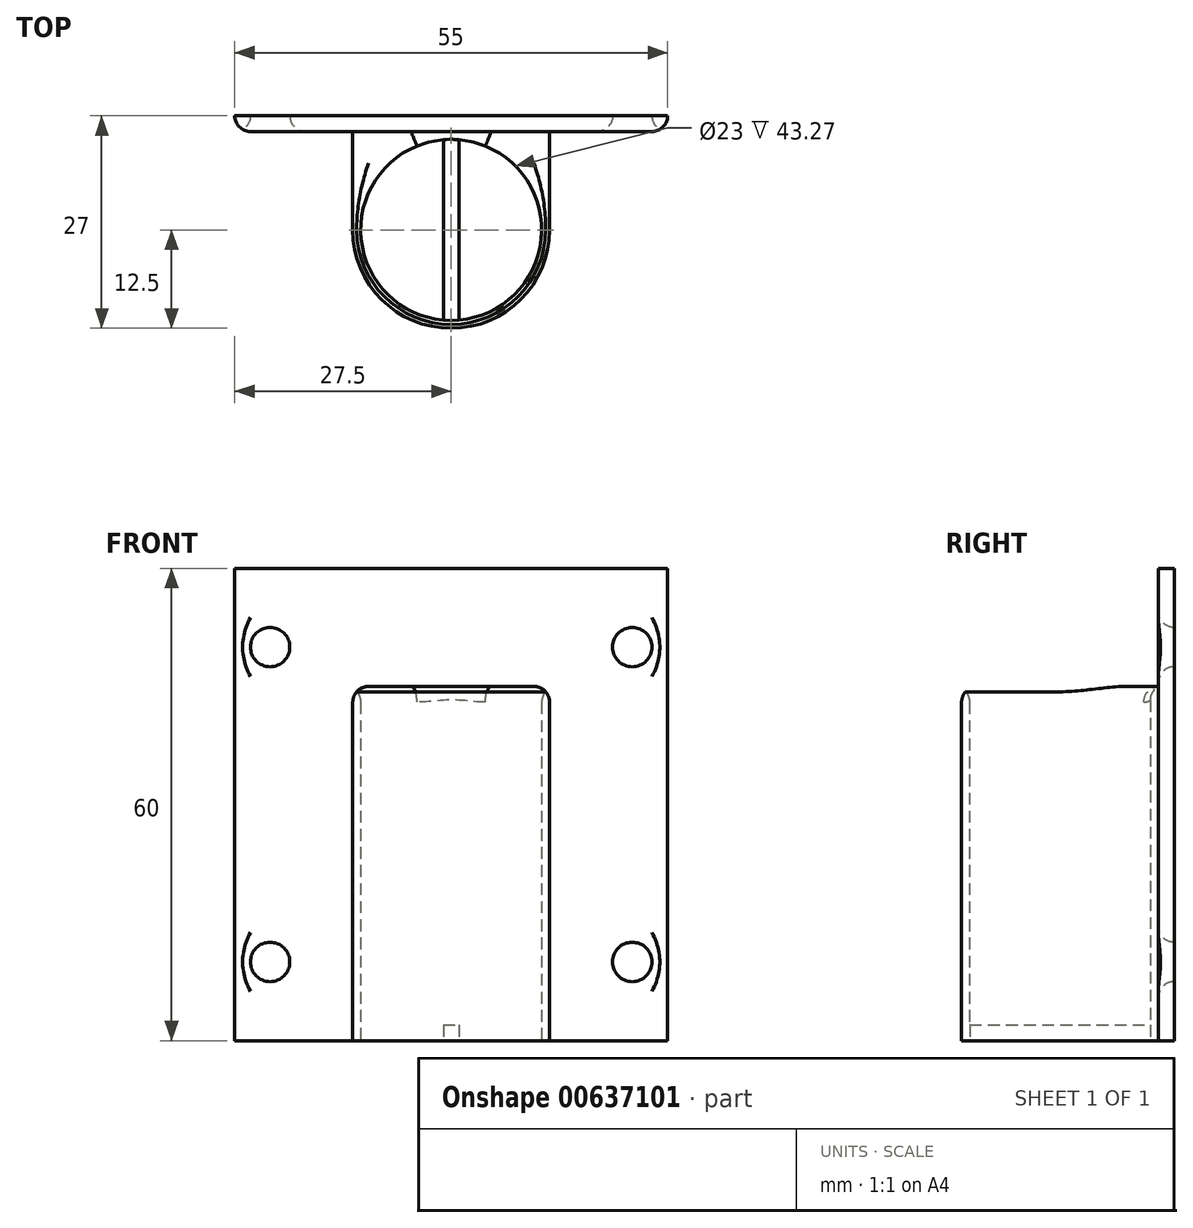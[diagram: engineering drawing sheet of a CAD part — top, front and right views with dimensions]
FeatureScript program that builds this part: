
annotation { "Feature Type Name" : "Feature", "Feature Type Description" : "" }
export const myFeature = defineFeature(function(context is Context, id is Id, definition is map)
    precondition{}
    {
        {
            var Q0;
            Q0=qCreatedBy(makeId("Top.planeOp"),FACE);
            var sketch = newSketch(context, id + "F0", { "sketchPlane" : qUnion([Q0])});
            skCircle(sketch, "E0", {"center": v(0, 0) * mm, "radius": 11.5 * mm});
            skCircle(sketch, "E1", {"center": v(0, 0) * mm, "radius": 12.5 * mm});
            skLineSegment(sketch, "E2", {"start": v(-12.5, 0) * mm, "end": v(-12.5, 14.5) * mm});
            skLineSegment(sketch, "E3", {"start": v(-12.5, 14.5) * mm, "end": v(27.5, 14.5) * mm});
            skLineSegment(sketch, "E4", {"start": v(12.5, 0) * mm, "end": v(12.5, 14.5) * mm});
            skLineSegment(sketch, "E5", {"start": v(-12.5, 14.5) * mm, "end": v(-27.5, 14.5) * mm});
            skLineSegment(sketch, "E6", {"start": v(-27.5, 14.5) * mm, "end": v(-27.5, 12.5) * mm});
            skLineSegment(sketch, "E7", {"start": v(27.5, 14.5) * mm, "end": v(27.5, 12.5) * mm});
            skLineSegment(sketch, "E8", {"start": v(-27.5, 12.5) * mm, "end": v(27.5, 12.5) * mm});
            skSolve(sketch);
        }
        {
            var Q0;
            {var subQ0=sQuery(id+"F0.wireOp",EDGE,"E5");Q0=makeQuery(id+"F0.imprint","IMPRINT",FACE,{"disambiguationData":[TD([[makeQuery(id+"F0.imprint","IMPRINT",EDGE,{"derivedFrom":subQ0}),1.0]])]});}
            var Q1;
            {var subQ4=sQuery(id+"F0.wireOp",EDGE,"E4");var subQ5=sQuery(id+"F0.wireOp",EDGE,"E3");var subQ6=makeQuery(id+"F0.imprint","INTERSECT",VERTEX,{"derivedFrom":[subQ5,subQ4]});Q1=makeQuery(id+"F0.imprint","IMPRINT",FACE,{"disambiguationData":[TD([[makeQuery(id+"F0.imprint","IMPRINT",EDGE,{"disambiguationData":[TD([[subQ6,1.0]])],"derivedFrom":subQ4}),1.0]])]});}
            var Q2;
            {var subQ0=sQuery(id+"F0.wireOp",EDGE,"E7");Q2=makeQuery(id+"F0.imprint","IMPRINT",FACE,{"disambiguationData":[TD([[makeQuery(id+"F0.imprint","IMPRINT",EDGE,{"derivedFrom":subQ0}),-1.0]])]});}
            var Q3;
            {var subQ0=sQuery(id+"F0.wireOp",EDGE,"E4");var subQ1=sQuery(id+"F0.wireOp",EDGE,"E1");var subQ2=makeQuery(id+"F0.imprint","INTERSECT",VERTEX,{"derivedFrom":[subQ1,subQ0]});Q3=makeQuery(id+"F0.imprint","IMPRINT",FACE,{"disambiguationData":[TD([[makeQuery(id+"F0.imprint","IMPRINT",EDGE,{"disambiguationData":[TD([[subQ2,-1.0]])],"derivedFrom":subQ1}),-1.0]])]});}
            var Q4;
            {var subQ0=sQuery(id+"F0.wireOp",EDGE,"E2");var subQ1=sQuery(id+"F0.wireOp",EDGE,"E1");var subQ2=makeQuery(id+"F0.imprint","INTERSECT",VERTEX,{"derivedFrom":[subQ1,subQ0]});Q4=makeQuery(id+"F0.imprint","IMPRINT",FACE,{"disambiguationData":[TD([[makeQuery(id+"F0.imprint","IMPRINT",EDGE,{"disambiguationData":[TD([[subQ2,1.0]])],"derivedFrom":subQ1}),-1.0]])]});}
            var Q5;
            Q5=makeQuery(id+"F0.imprint","IMPRINT",FACE,{"disambiguationData":[TD([[makeQuery(id+"F0.imprint","IMPRINT",EDGE,{"derivedFrom":sQuery(id+"F0.wireOp",EDGE,"E0")}),-1.0]])]});
            extrude(context, id + "F1", {"entities" : qUnion([Q0, Q1, Q2, Q3, Q4, Q5]), "depth" : 45 * mm, "offsetDistance" : 25 * mm});
        }
        {
            var Q0;
            Q0=makeQuery(id+"F1.opExtrude","CAP_FACE",FACE,{"disambiguationData":[OSD([sQuery(id+"F0.wireOp",EDGE,"E0"),sQuery(id+"F0.wireOp",EDGE,"E1"),sQuery(id+"F0.wireOp",EDGE,"E2"),sQuery(id+"F0.wireOp",EDGE,"E3"),sQuery(id+"F0.wireOp",EDGE,"E4"),sQuery(id+"F0.wireOp",EDGE,"E5"),sQuery(id+"F0.wireOp",EDGE,"E6"),sQuery(id+"F0.wireOp",EDGE,"E7"),sQuery(id+"F0.wireOp",EDGE,"E8")])],"isStart":false});
            var sketch = newSketch(context, id + "F2", { "sketchPlane" : qUnion([Q0])});
            skLineSegment(sketch, "E9", {"start": v(-27.5, 14.5) * mm, "end": v(27.5, 14.5) * mm});
            skLineSegment(sketch, "E10", {"start": v(27.5, 14.5) * mm, "end": v(27.5, 12.5) * mm});
            skLineSegment(sketch, "E11", {"start": v(27.5, 12.5) * mm, "end": v(-27.5, 12.5) * mm});
            skLineSegment(sketch, "E12", {"start": v(-27.5, 12.5) * mm, "end": v(-27.5, 14.5) * mm});
            skSolve(sketch);
        }
        {
            var Q0;
            Q0=makeQuery(id+"F2.imprint","IMPRINT",FACE,{"disambiguationData":[TD([[makeQuery(id+"F2.imprint","IMPRINT",EDGE,{"derivedFrom":sQuery(id+"F2.wireOp",EDGE,"E9")}),1.0]])]});
            extrude(context, id + "F3", {"entities" : qUnion([Q0]), "operationType" : NewBodyOperationType.ADD, "depth" : 15 * mm, "offsetDistance" : 25 * mm});
        }
        {
            var Q0;
            Q0=makeQuery(id+"F1.opExtrude","SWEPT_FACE",FACE,{"disambiguationData":[OSD([sQuery(id+"F0.wireOp",EDGE,"E3"),sQuery(id+"F0.wireOp",EDGE,"E5")])]});
            var sketch = newSketch(context, id + "F4", { "sketchPlane" : qUnion([Q0])});
            skCircle(sketch, "E13", {"center": v(-23, 50) * mm, "radius": 2.5 * mm});
            skCircle(sketch, "E14", {"center": v(23, 50) * mm, "radius": 2.5 * mm});
            skCircle(sketch, "E15", {"center": v(-23, 10) * mm, "radius": 2.5 * mm});
            skCircle(sketch, "E16", {"center": v(23, 10) * mm, "radius": 2.5 * mm});
            skSolve(sketch);
        }
        {
            var Q0;
            Q0 = qSketchRegion(id + "F4", true);
            extrude(context, id + "F5", {"entities" : qUnion([Q0]), "operationType" : NewBodyOperationType.REMOVE, "oppositeDirection" : true, "depth" : 25 * mm, "offsetDistance" : 25 * mm});
        }
        {
            var Q0;
            Q0=makeQuery(id+"F1.opExtrude","CAP_EDGE",EDGE,{"disambiguationData":[OSD([sQuery(id+"F0.wireOp",EDGE,"E0")])],"isStart":false});
            var Q1;
            Q1=makeQuery(id+"F1.opExtrude","CAP_EDGE",EDGE,{"disambiguationData":[OSD([sQuery(id+"F0.wireOp",EDGE,"E2")])],"isStart":false});
            var Q2;
            Q2=makeQuery(id+"F1.opExtrude","CAP_EDGE",EDGE,{"disambiguationData":[OSD([sQuery(id+"F0.wireOp",EDGE,"E1")])],"isStart":false});
            var Q3;
            {var subQ0=sQuery(id+"F0.wireOp",EDGE,"E8");Q3=makeQuery(id+"F1.opExtrude","CAP_EDGE",EDGE,{"disambiguationData":[OSD([subQ0]),TDD([makeQuery(id+"F0.imprint","IMPRINT",EDGE,{"disambiguationData":[TD([[makeQuery(id+"F0.imprint","INTERSECT",VERTEX,{"derivedFrom":[sQuery(id+"F0.wireOp",EDGE,"E6"),subQ0]}),-1.0]])],"derivedFrom":subQ0})])],"isStart":false});}
            var Q4;
            Q4=makeQuery(id+"F1.opExtrude","CAP_EDGE",EDGE,{"disambiguationData":[OSD([sQuery(id+"F0.wireOp",EDGE,"E6")])],"isStart":false});
            var Q5;
            {var subQ0=sQuery(id+"F0.wireOp",EDGE,"E8");Q5=makeQuery(id+"F1.opExtrude","CAP_EDGE",EDGE,{"disambiguationData":[OSD([subQ0]),TDD([makeQuery(id+"F0.imprint","IMPRINT",EDGE,{"disambiguationData":[TD([[makeQuery(id+"F0.imprint","INTERSECT",VERTEX,{"derivedFrom":[sQuery(id+"F0.wireOp",EDGE,"E7"),subQ0]}),1.0]])],"derivedFrom":subQ0})])],"isStart":false});}
            var Q6;
            Q6=makeQuery(id+"F1.opExtrude","CAP_EDGE",EDGE,{"disambiguationData":[OSD([sQuery(id+"F0.wireOp",EDGE,"E4")])],"isStart":false});
            var Q7;
            Q7=makeQuery(id+"F1.opExtrude","CAP_EDGE",EDGE,{"disambiguationData":[OSD([sQuery(id+"F0.wireOp",EDGE,"E7")])],"isStart":false});
            var Q8;
            Q8=makeQuery(id+"F1.opExtrude","SWEPT_EDGE",EDGE,{"disambiguationData":[OSD([sQuery(id+"F0.wireOp",EDGE,"E7"),sQuery(id+"F0.wireOp",EDGE,"E8")])]});
            var Q9;
            Q9=makeQuery(id+"F1.opExtrude","SWEPT_EDGE",EDGE,{"disambiguationData":[OSD([sQuery(id+"F0.wireOp",EDGE,"E6"),sQuery(id+"F0.wireOp",EDGE,"E8")])]});
            var Q10;
            {var subQ0=sQuery(id+"F0.wireOp",EDGE,"E8");Q10=makeQuery(id+"F5.boolean.opBoolean","INTERSECT",EDGE,{"derivedFrom":[makeQuery(id+"F1.opExtrude","SWEPT_FACE",FACE,{"disambiguationData":[OSD([subQ0]),TDD([makeQuery(id+"F0.imprint","IMPRINT",EDGE,{"disambiguationData":[TD([[makeQuery(id+"F0.imprint","INTERSECT",VERTEX,{"derivedFrom":[sQuery(id+"F0.wireOp",EDGE,"E6"),subQ0]}),-1.0]])],"derivedFrom":subQ0})])]}),makeQuery(id+"F5.opExtrude","SWEPT_FACE",FACE,{"disambiguationData":[OSD([sQuery(id+"F4.wireOp",EDGE,"E14")])]})]});}
            var Q11;
            {var subQ0=sQuery(id+"F0.wireOp",EDGE,"E8");Q11=makeQuery(id+"F5.boolean.opBoolean","INTERSECT",EDGE,{"derivedFrom":[makeQuery(id+"F1.opExtrude","SWEPT_FACE",FACE,{"disambiguationData":[OSD([subQ0]),TDD([makeQuery(id+"F0.imprint","IMPRINT",EDGE,{"disambiguationData":[TD([[makeQuery(id+"F0.imprint","INTERSECT",VERTEX,{"derivedFrom":[sQuery(id+"F0.wireOp",EDGE,"E6"),subQ0]}),-1.0]])],"derivedFrom":subQ0})])]}),makeQuery(id+"F5.opExtrude","SWEPT_FACE",FACE,{"disambiguationData":[OSD([sQuery(id+"F4.wireOp",EDGE,"E16")])]})]});}
            var Q12;
            {var subQ0=sQuery(id+"F0.wireOp",EDGE,"E8");Q12=makeQuery(id+"F5.boolean.opBoolean","INTERSECT",EDGE,{"derivedFrom":[makeQuery(id+"F1.opExtrude","SWEPT_FACE",FACE,{"disambiguationData":[OSD([subQ0]),TDD([makeQuery(id+"F0.imprint","IMPRINT",EDGE,{"disambiguationData":[TD([[makeQuery(id+"F0.imprint","INTERSECT",VERTEX,{"derivedFrom":[sQuery(id+"F0.wireOp",EDGE,"E7"),subQ0]}),1.0]])],"derivedFrom":subQ0})])]}),makeQuery(id+"F5.opExtrude","SWEPT_FACE",FACE,{"disambiguationData":[OSD([sQuery(id+"F4.wireOp",EDGE,"E15")])]})]});}
            var Q13;
            {var subQ0=sQuery(id+"F0.wireOp",EDGE,"E8");Q13=makeQuery(id+"F5.boolean.opBoolean","INTERSECT",EDGE,{"derivedFrom":[makeQuery(id+"F1.opExtrude","SWEPT_FACE",FACE,{"disambiguationData":[OSD([subQ0]),TDD([makeQuery(id+"F0.imprint","IMPRINT",EDGE,{"disambiguationData":[TD([[makeQuery(id+"F0.imprint","INTERSECT",VERTEX,{"derivedFrom":[sQuery(id+"F0.wireOp",EDGE,"E7"),subQ0]}),1.0]])],"derivedFrom":subQ0})])]}),makeQuery(id+"F5.opExtrude","SWEPT_FACE",FACE,{"disambiguationData":[OSD([sQuery(id+"F4.wireOp",EDGE,"E13")])]})]});}
            fillet(context, id + "F6", {"entities" : qUnion([Q0, Q1, Q2, Q3, Q4, Q5, Q6, Q7, Q8, Q9, Q10, Q11, Q12, Q13]), "radius" : 2 * mm, "tangentPropagation" : true, "allowEdgeOverflow" : false});
        }
        {
            var Q0;
            Q0=qCreatedBy(makeId("Top.planeOp"),FACE);
            var sketch = newSketch(context, id + "F7", { "sketchPlane" : qUnion([Q0])});
            skLineSegment(sketch, "E17", {"start": v(0, -11.5) * mm, "end": v(-1, -11.5) * mm});
            skLineSegment(sketch, "E18", {"start": v(-1, -11.5) * mm, "end": v(-1, 12.5) * mm});
            skLineSegment(sketch, "E19", {"start": v(-1, 12.5) * mm, "end": v(0, 12.5) * mm});
            skLineSegment(sketch, "E20.MirrorCS", {"start": v(1, -11.5) * mm, "end": v(1, 12.5) * mm});
            skLineSegment(sketch, "E21.MirrorCS", {"start": v(0, -11.5) * mm, "end": v(1, -11.5) * mm});
            skLineSegment(sketch, "E22.MirrorCS", {"start": v(1, 12.5) * mm, "end": v(0, 12.5) * mm});
            skSolve(sketch);
        }
        {
            var Q0;
            Q0=makeQuery(id+"F7.imprint","IMPRINT",FACE,{"disambiguationData":[TD([[makeQuery(id+"F7.imprint","IMPRINT",EDGE,{"derivedFrom":sQuery(id+"F7.wireOp",EDGE,"E17")}),-1.0]])]});
            extrude(context, id + "F8", {"entities" : qUnion([Q0]), "operationType" : NewBodyOperationType.ADD, "depth" : 2 * mm, "offsetDistance" : 25 * mm});
        }
    });
